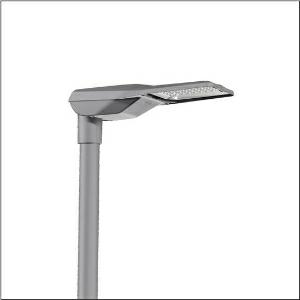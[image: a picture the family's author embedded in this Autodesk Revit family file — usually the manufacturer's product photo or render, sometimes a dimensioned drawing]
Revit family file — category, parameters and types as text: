
# Revit family: streetlight_sl_21_iq_mini___p0_5a_5xe2v31d08hb_68d8
name_source: partatom
category: Lighting Fixtures
units: mm (PartAtom-declared; Revit-internal decimal feet)

## family parameters
Cut with Voids When Loaded = No
Host = Face
Light Source = No
Part Type = Normal
Room Calculation Point = No
Round Connector Dimension = Use Diameter
Shared = No

## types (1)
- --- (1 x LED, 9290 lm, 70.9 W, 3000K)
    Apparent Load = 71 VA
    CIE Flux Codes = 37 73 96 100 100
    Color Rendering = 70
    Color Temperature = 3000K
    Default Elevation = 1800 mm
    Description = Streetlight SL 21 iQ mini, mast luminaire, primary light control with lens, of PMMA, primary optical cover: cover, of toughened safety glass, transparent, light distribution: P0.5a, light emission: direct distribution, primary light characteristic: asymmetric, installation type: post-top, side-entry, LED, High Power LED, rated luminous flux: 9.290lm, luminous efficacy: 131lm/W, light colour: 730, colour temperature: 3000K, control gear: iQ-Comfort, control: pre-setting: linear dimming characteristic, Auto-Match, Temp-Guard, Lumen-Switch, Night-Set, Smart-Wire, Light-Fading, Desk-Remote (wireless, voltage-free reading and setting of iQ features in the workshop via application-optimized NFC function/RFID function), optimised constant luminous flux control (CLO 2.0), mains connection: 220..240V, AC, 50/60Hz, start of lifetime: 71W, end of service life: 75W, reduction: 31W, luminaire housing, of diecast aluminium, powder-coated, SITECO metallic grey (DB 702S), corrosivity category C5 high according to DIN EN ISO 12944, please order mast flange separately, inclination adjustable: 0°, 5°, 10°, 15°, sealing non-destructively replaceable, multi-level sealing system, length: 628mm, width: 235mm, height: 110mm, mast flange for spigot size: 42mm (side-entry): 5XC10008XM4, 60/48mm (side-entry/post-top): 5XC10108XM2, 76/60mm (side-entry/post-top): 5XC10108XM1, mounting height: 4..8m, protection rating (complete): IP66, insulation class (complete): insulation class II (safety insulation), certification: CE, ENEC, ENEC+, VDE, impact resistance: IK10, permissible operating ambient temperature for outdoor applications: -40..+50°C, standard-compliant lighting for roads and squares, packaging unit: 1 piece

Light Distribution: P0.5a
    Height = 110 mm
    Lamp = 1 x LED
    Lamp Light Flux = 9290 lm
    Lamp Power = 70.9 W
    Lamp count = 1
    Length = 625 mm
    Luminous efficacy = 131 lm/W
    Manufacturer = Siteco
    ModVariant = No
    Model = 5XE2V31D08HB
    Number of Poles = 1
    OnlyDefault = Yes
    Power Factor = 1
    Product Name = Streetlight SL 21 iQ mini | P0.5a
    Product group = mast luminaire | pylon top
    ProductGroupID = 6100
    Protection Class = Protection class II
    Protection Degree = IP 66
    RLX_Detail_Level = 1
    RLX_Emergency_Light_Flux = 0 lm
    RLX_Emergency_Type = 0
    RLX_Emergency_Type_DB = No
    RlxData = <blob elided: 92009 chars, md5=65bc8943>
    Socket = socket
    Standby Power = 0 W
    System Light Flux = 9290 lm
    System Power = 71 W
    Type Comments = factory setting: luminous flux: 100 % | dim-lin: 254 | 711 mA
    Type Image = l_1003519.jpg
    URL = http://relux.com
    VarID = @adj_077471
    Voltage = 0 V
    Weight = 0.00 kg
    Width = 234 mm

## geometry (parser evidence)
native form markers: Blend x4, Sweep x11
no freeform markers — native parametric forms only
